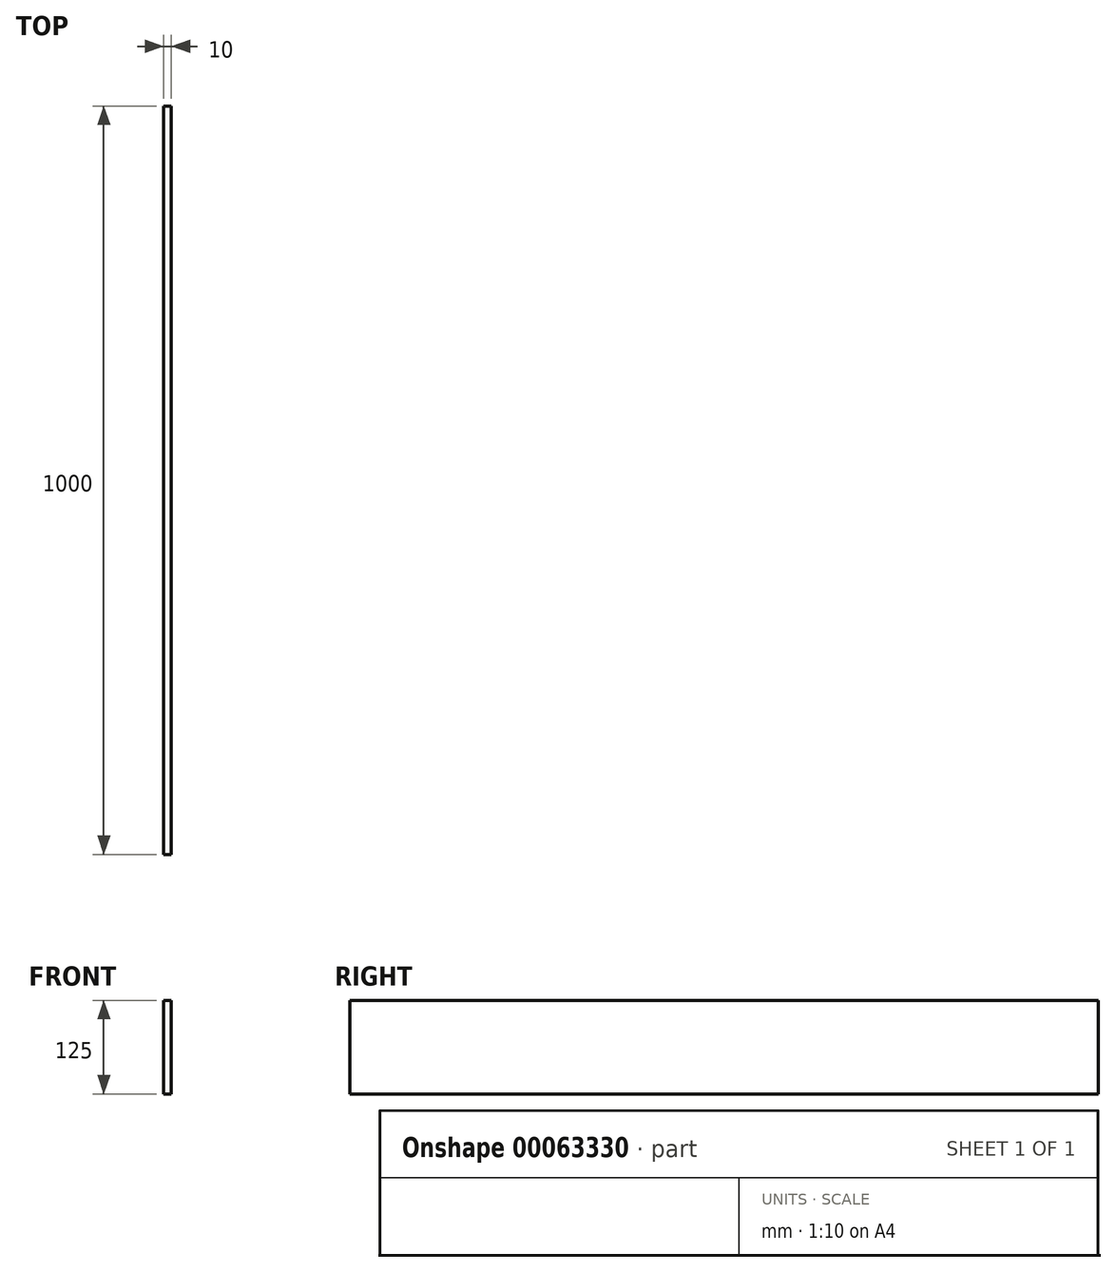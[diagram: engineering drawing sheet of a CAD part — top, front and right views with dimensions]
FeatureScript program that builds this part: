
annotation { "Feature Type Name" : "Feature", "Feature Type Description" : "" }
export const myFeature = defineFeature(function(context is Context, id is Id, definition is map)
    precondition{}
    {
        {
            var Q0;
            Q0=qCreatedBy(makeId("Right.planeOp"),FACE);
            var sketch = newSketch(context, id + "F0", { "sketchPlane" : qUnion([Q0])});
            skLineSegment(sketch, "E0.rect.bottom", {"start": v(500, 62.5) * mm, "end": v(-500, 62.5) * mm});
            skLineSegment(sketch, "E0.rect.top", {"start": v(500, -62.5) * mm, "end": v(-500, -62.5) * mm});
            skLineSegment(sketch, "E0.rect.left", {"start": v(500, 62.5) * mm, "end": v(500, -62.5) * mm});
            skLineSegment(sketch, "E0.rect.right", {"start": v(-500, 62.5) * mm, "end": v(-500, -62.5) * mm});
            skPoint(sketch, "E0.rect.middle", {"position": v(0, 0) * mm});
            skSolve(sketch);
        }
        {
            var Q0;
            Q0=makeQuery(id+"F0.imprint","IMPRINT",FACE,{"disambiguationData":[TD([[makeQuery(id+"F0.imprint","IMPRINT",EDGE,{"derivedFrom":sQuery(id+"F0.wireOp",EDGE,"E0.rect.bottom")}),1.0]])]});
            extrude(context, id + "F1", {"entities" : qUnion([Q0]), "depth" : 10 * mm});
        }
    });
